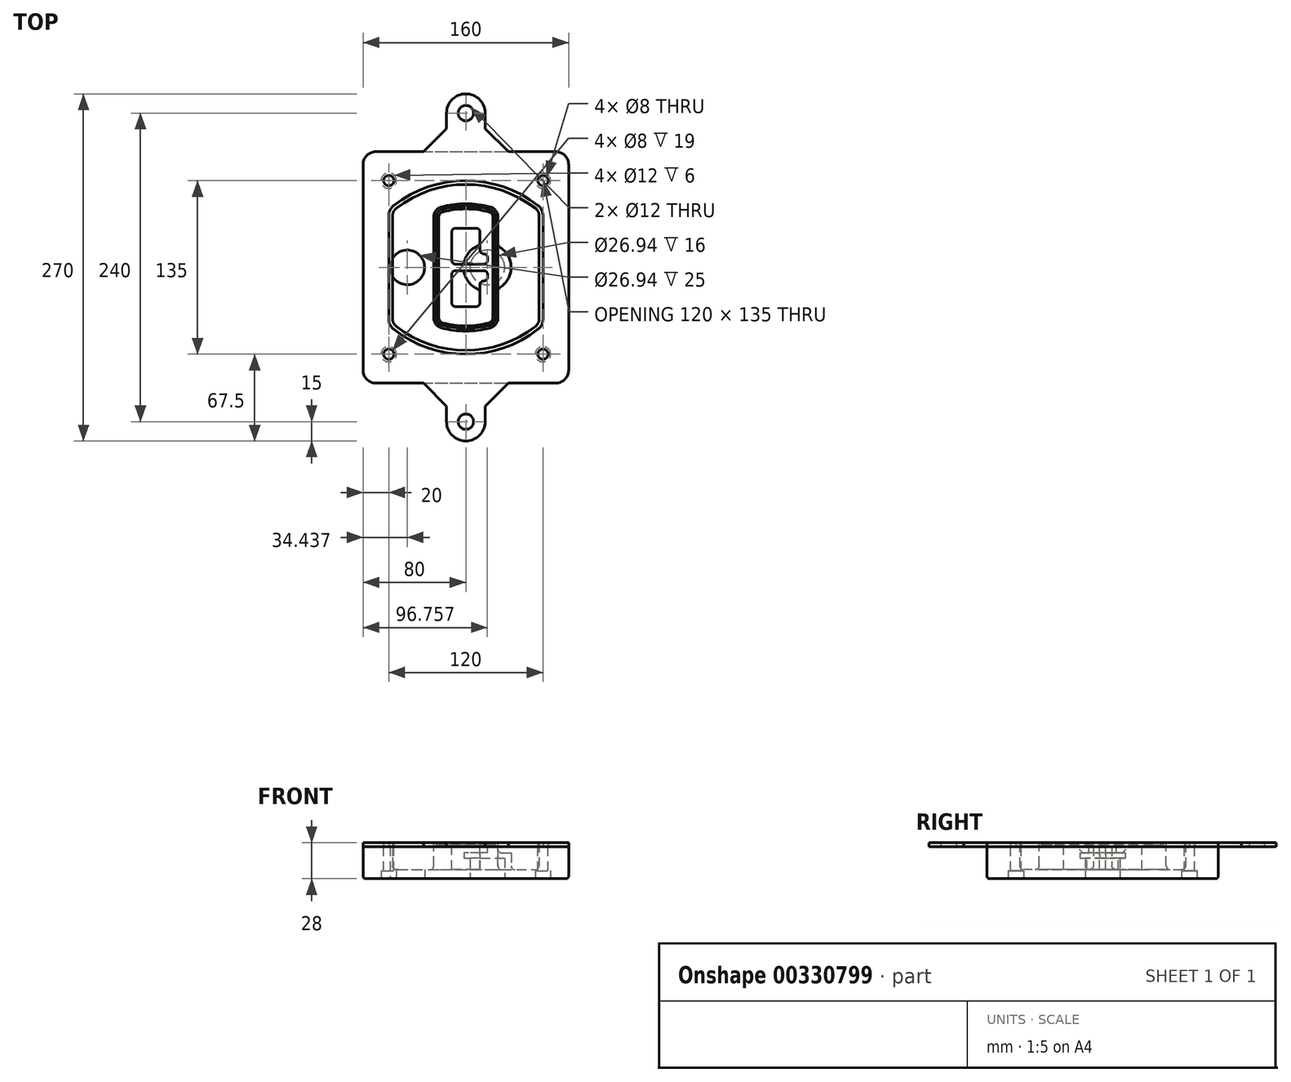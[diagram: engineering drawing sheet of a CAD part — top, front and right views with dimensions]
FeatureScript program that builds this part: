
annotation { "Feature Type Name" : "Feature", "Feature Type Description" : "" }
export const myFeature = defineFeature(function(context is Context, id is Id, definition is map)
    precondition{}
    {
        {
            var Q0;
            Q0=qCreatedBy(makeId("Top.planeOp"),FACE);
            var sketch = newSketch(context, id + "F0", { "sketchPlane" : qUnion([Q0])});
            skPoint(sketch, "E0.rect.middle", {"position": v(0, 0) * mm});
            skLineSegment(sketch, "E1.bottom", {"start": v(-70, -90) * mm, "end": v(70, -90) * mm});
            skLineSegment(sketch, "E1.top", {"start": v(-70, 90) * mm, "end": v(70, 90) * mm});
            skLineSegment(sketch, "E1.left", {"start": v(-80, -80) * mm, "end": v(-80, 80) * mm});
            skLineSegment(sketch, "E1.right", {"start": v(80, -80) * mm, "end": v(80, 80) * mm});
            skLineSegment(sketch, "E2", {"start": v(-80, 90) * mm, "end": v(80, -90) * mm, "construction": true});
            skLineSegment(sketch, "E3", {"start": v(80, 90) * mm, "end": v(-80, -90) * mm, "construction": true});
            skCircle(sketch, "E4", {"center": v(-60, 67.5) * mm, "radius": 4 * mm});
            skCircle(sketch, "E5", {"center": v(60, 67.5) * mm, "radius": 4 * mm});
            skCircle(sketch, "E6", {"center": v(60, -67.5) * mm, "radius": 4 * mm});
            skCircle(sketch, "E7", {"center": v(-60, -67.5) * mm, "radius": 4 * mm});
            skLineSegment(sketch, "E8", {"start": v(-60, 67.5) * mm, "end": v(60, 67.5) * mm, "construction": true});
            skLineSegment(sketch, "E9", {"start": v(60, 67.5) * mm, "end": v(60, -67.5) * mm, "construction": true});
            skLineSegment(sketch, "E10", {"start": v(60, -67.5) * mm, "end": v(-60, -67.5) * mm, "construction": true});
            skLineSegment(sketch, "E11", {"start": v(-60, -67.5) * mm, "end": v(-60, 67.5) * mm, "construction": true});
            skLineSegment(sketch, "E12", {"start": v(-60, 40.3) * mm, "end": v(-60, -40.3) * mm});
            skLineSegment(sketch, "E13", {"start": v(60, 40.3) * mm, "end": v(60, -40.3) * mm});
            skArc(sketch, "E14", {"start": v(56.15, 48.18) * mm, "mid": v(0, 67.5) * mm, "end": v(-56.15, 48.18) * mm});
            skArc(sketch, "E15", {"start": v(-56.15, -48.18) * mm, "mid": v(0, -67.5) * mm, "end": v(56.15, -48.18) * mm});
            skLineSegment(sketch, "E16", {"start": v(-60, 0) * mm, "end": v(60, 0) * mm, "construction": true});
            skPoint(sketch, "E17.visualSharp", {"position": v(-60, -45) * mm});
            skArc(sketch, "E17.filletArc", {"start": v(-60, -40.3) * mm, "mid": v(-58.99, -44.68) * mm, "end": v(-56.15, -48.18) * mm});
            skPoint(sketch, "E18.visualSharp", {"position": v(-60, 45) * mm});
            skArc(sketch, "E18.filletArc", {"start": v(-56.15, 48.18) * mm, "mid": v(-58.99, 44.68) * mm, "end": v(-60, 40.3) * mm});
            skPoint(sketch, "E19.visualSharp", {"position": v(60, 45) * mm});
            skArc(sketch, "E19.filletArc", {"start": v(60, 40.3) * mm, "mid": v(58.99, 44.68) * mm, "end": v(56.15, 48.18) * mm});
            skPoint(sketch, "E20.visualSharp", {"position": v(60, -45) * mm});
            skArc(sketch, "E20.filletArc", {"start": v(56.15, -48.18) * mm, "mid": v(58.99, -44.68) * mm, "end": v(60, -40.3) * mm});
            skPoint(sketch, "E21.visualSharp", {"position": v(-80, 90) * mm});
            skArc(sketch, "E21.filletArc", {"start": v(-70, 90) * mm, "mid": v(-77.07, 87.07) * mm, "end": v(-80, 80) * mm});
            skPoint(sketch, "E22.visualSharp", {"position": v(80, 90) * mm});
            skArc(sketch, "E22.filletArc", {"start": v(80, 80) * mm, "mid": v(77.07, 87.07) * mm, "end": v(70, 90) * mm});
            skPoint(sketch, "E23.visualSharp", {"position": v(80, -90) * mm});
            skArc(sketch, "E23.filletArc", {"start": v(70, -90) * mm, "mid": v(77.07, -87.07) * mm, "end": v(80, -80) * mm});
            skPoint(sketch, "E24.visualSharp", {"position": v(-80, -90) * mm});
            skArc(sketch, "E24.filletArc", {"start": v(-80, -80) * mm, "mid": v(-77.07, -87.07) * mm, "end": v(-70, -90) * mm});
            skArc(sketch, "E25.0", {"start": v(57, 40.3) * mm, "mid": v(56.3, 43.36) * mm, "end": v(54.3, 45.81) * mm});
            skLineSegment(sketch, "E25.1", {"start": v(57, 40.3) * mm, "end": v(57, -40.3) * mm});
            skArc(sketch, "E25.2", {"start": v(54.3, -45.81) * mm, "mid": v(56.3, -43.36) * mm, "end": v(57, -40.3) * mm});
            skArc(sketch, "E25.3", {"start": v(-54.3, -45.81) * mm, "mid": v(0, -64.5) * mm, "end": v(54.3, -45.81) * mm});
            skArc(sketch, "E25.4", {"start": v(-57, -40.3) * mm, "mid": v(-56.3, -43.36) * mm, "end": v(-54.3, -45.81) * mm});
            skArc(sketch, "E25.5", {"start": v(54.3, 45.81) * mm, "mid": v(0, 64.5) * mm, "end": v(-54.3, 45.81) * mm});
            skLineSegment(sketch, "E25.6", {"start": v(-57, 40.3) * mm, "end": v(-57, -40.3) * mm});
            skArc(sketch, "E25.7", {"start": v(-54.3, 45.81) * mm, "mid": v(-56.3, 43.36) * mm, "end": v(-57, 40.3) * mm});
            skArc(sketch, "E26.0", {"start": v(-58.62, 51.33) * mm, "mid": v(-62.58, 46.43) * mm, "end": v(-64, 40.3) * mm});
            skArc(sketch, "E26.1", {"start": v(58.62, 51.33) * mm, "mid": v(0, 71.5) * mm, "end": v(-58.62, 51.33) * mm});
            skArc(sketch, "E26.2", {"start": v(64, 40.3) * mm, "mid": v(62.58, 46.43) * mm, "end": v(58.62, 51.33) * mm});
            skLineSegment(sketch, "E26.3", {"start": v(64, 40.3) * mm, "end": v(64, -40.3) * mm});
            skArc(sketch, "E26.4", {"start": v(58.62, -51.33) * mm, "mid": v(62.58, -46.43) * mm, "end": v(64, -40.3) * mm});
            skLineSegment(sketch, "E26.5", {"start": v(-64, 40.3) * mm, "end": v(-64, -40.3) * mm});
            skArc(sketch, "E26.6", {"start": v(-58.62, -51.33) * mm, "mid": v(0, -71.5) * mm, "end": v(58.62, -51.33) * mm});
            skArc(sketch, "E26.7", {"start": v(-64, -40.3) * mm, "mid": v(-62.58, -46.43) * mm, "end": v(-58.62, -51.33) * mm});
            skSolve(sketch);
        }
        {
            var Q0;
            Q0=makeQuery(id+"F0.imprint","IMPRINT",FACE,{"disambiguationData":[TD([[makeQuery(id+"F0.imprint","IMPRINT",EDGE,{"derivedFrom":sQuery(id+"F0.wireOp",EDGE,"E1.bottom")}),1.0]])]});
            var Q1;
            Q1=makeQuery(id+"F0.imprint","IMPRINT",FACE,{"disambiguationData":[TD([[makeQuery(id+"F0.imprint","IMPRINT",EDGE,{"derivedFrom":sQuery(id+"F0.wireOp",EDGE,"E12")}),1.0]])]});
            var Q2;
            Q2=makeQuery(id+"F0.imprint","IMPRINT",FACE,{"disambiguationData":[TD([[makeQuery(id+"F0.imprint","IMPRINT",EDGE,{"derivedFrom":sQuery(id+"F0.wireOp",EDGE,"E25.0")}),1.0]])]});
            var Q3;
            Q3=makeQuery(id+"F0.imprint","IMPRINT",FACE,{"disambiguationData":[TD([[makeQuery(id+"F0.imprint","IMPRINT",EDGE,{"derivedFrom":sQuery(id+"F0.wireOp",EDGE,"E12")}),-1.0]])]});
            extrude(context, id + "F1", {"entities" : qUnion([Q0, Q1, Q2, Q3]), "oppositeDirection" : true, "depth" : 25 * mm});
        }
        {
            var Q0;
            Q0=makeQuery(id+"F0.imprint","IMPRINT",FACE,{"disambiguationData":[TD([[makeQuery(id+"F0.imprint","IMPRINT",EDGE,{"derivedFrom":sQuery(id+"F0.wireOp",EDGE,"E12")}),1.0]])]});
            extrude(context, id + "F2", {"entities" : qUnion([Q0]), "operationType" : NewBodyOperationType.ADD, "depth" : 3 * mm});
        }
        {
            var Q0;
            Q0=makeQuery(id+"F0.imprint","IMPRINT",FACE,{"disambiguationData":[TD([[makeQuery(id+"F0.imprint","IMPRINT",EDGE,{"derivedFrom":sQuery(id+"F0.wireOp",EDGE,"E25.0")}),1.0]])]});
            extrude(context, id + "F3", {"entities" : qUnion([Q0]), "operationType" : NewBodyOperationType.REMOVE, "oppositeDirection" : true, "depth" : 18 * mm});
        }
        {
            var Q0;
            Q0=makeQuery(id+"F2.opExtrude","CAP_FACE",FACE,{"disambiguationData":[OSD([sQuery(id+"F0.wireOp",EDGE,"E12"),sQuery(id+"F0.wireOp",EDGE,"E13"),sQuery(id+"F0.wireOp",EDGE,"E14"),sQuery(id+"F0.wireOp",EDGE,"E15"),sQuery(id+"F0.wireOp",EDGE,"E17.filletArc"),sQuery(id+"F0.wireOp",EDGE,"E18.filletArc"),sQuery(id+"F0.wireOp",EDGE,"E19.filletArc"),sQuery(id+"F0.wireOp",EDGE,"E20.filletArc"),sQuery(id+"F0.wireOp",EDGE,"E25.0"),sQuery(id+"F0.wireOp",EDGE,"E25.1"),sQuery(id+"F0.wireOp",EDGE,"E25.2"),sQuery(id+"F0.wireOp",EDGE,"E25.3"),sQuery(id+"F0.wireOp",EDGE,"E25.4"),sQuery(id+"F0.wireOp",EDGE,"E25.5"),sQuery(id+"F0.wireOp",EDGE,"E25.6"),sQuery(id+"F0.wireOp",EDGE,"E25.7")])],"isStart":false});
            var sketch = newSketch(context, id + "F4", { "sketchPlane" : qUnion([Q0])});
            skArc(sketch, "E27.0", {"start": v(-19.08, -46.97) * mm, "mid": v(0, -49.5) * mm, "end": v(19.08, -46.97) * mm});
            skArc(sketch, "E28.0", {"start": v(19.08, 46.97) * mm, "mid": v(0, 49.5) * mm, "end": v(-19.08, 46.97) * mm});
            skLineSegment(sketch, "E29", {"start": v(-25, 39.25) * mm, "end": v(-25, -39.25) * mm});
            skLineSegment(sketch, "E30", {"start": v(25, 39.25) * mm, "end": v(25, -39.25) * mm});
            skLineSegment(sketch, "E31", {"start": v(-25, 45.1) * mm, "end": v(25, 45.1) * mm, "construction": true});
            skLineSegment(sketch, "E32", {"start": v(-25, -45.1) * mm, "end": v(25, -45.1) * mm, "construction": true});
            skPoint(sketch, "E33.visualSharp", {"position": v(-25, 45.1) * mm});
            skArc(sketch, "E33.filletArc", {"start": v(-19.08, 46.97) * mm, "mid": v(-23.35, 44.11) * mm, "end": v(-25, 39.25) * mm});
            skPoint(sketch, "E34.visualSharp", {"position": v(25, 45.1) * mm});
            skArc(sketch, "E34.filletArc", {"start": v(25, 39.25) * mm, "mid": v(23.35, 44.11) * mm, "end": v(19.08, 46.97) * mm});
            skPoint(sketch, "E35.visualSharp", {"position": v(25, -45.1) * mm});
            skArc(sketch, "E35.filletArc", {"start": v(19.08, -46.97) * mm, "mid": v(23.35, -44.11) * mm, "end": v(25, -39.25) * mm});
            skPoint(sketch, "E36.visualSharp", {"position": v(-25, -45.1) * mm});
            skArc(sketch, "E36.filletArc", {"start": v(-25, -39.25) * mm, "mid": v(-23.35, -44.11) * mm, "end": v(-19.08, -46.97) * mm});
            skArc(sketch, "E37.0", {"start": v(54.3, 45.81) * mm, "mid": v(0, 64.5) * mm, "end": v(-54.3, 45.81) * mm});
            skArc(sketch, "E37.1", {"start": v(-54.3, 45.81) * mm, "mid": v(-56.3, 43.36) * mm, "end": v(-57, 40.3) * mm});
            skLineSegment(sketch, "E37.2", {"start": v(-57, 40.3) * mm, "end": v(-57, -40.3) * mm});
            skArc(sketch, "E37.3", {"start": v(-57, -40.3) * mm, "mid": v(-56.3, -43.36) * mm, "end": v(-54.3, -45.81) * mm});
            skArc(sketch, "E37.4", {"start": v(-54.3, -45.81) * mm, "mid": v(0, -64.5) * mm, "end": v(54.3, -45.81) * mm});
            skArc(sketch, "E37.5", {"start": v(54.3, -45.81) * mm, "mid": v(56.3, -43.36) * mm, "end": v(57, -40.3) * mm});
            skLineSegment(sketch, "E37.6", {"start": v(57, 40.3) * mm, "end": v(57, -40.3) * mm});
            skArc(sketch, "E37.7", {"start": v(57, 40.3) * mm, "mid": v(56.3, 43.36) * mm, "end": v(54.3, 45.81) * mm});
            skLineSegment(sketch, "E38.0", {"start": v(23, 39.25) * mm, "end": v(23, -39.25) * mm});
            skArc(sketch, "E38.1", {"start": v(18.56, -45.04) * mm, "mid": v(21.76, -42.9) * mm, "end": v(23, -39.25) * mm});
            skArc(sketch, "E38.2", {"start": v(-18.56, -45.04) * mm, "mid": v(0, -47.5) * mm, "end": v(18.56, -45.04) * mm});
            skArc(sketch, "E38.3", {"start": v(-23, -39.25) * mm, "mid": v(-21.76, -42.9) * mm, "end": v(-18.56, -45.04) * mm});
            skLineSegment(sketch, "E38.4", {"start": v(-23, 39.25) * mm, "end": v(-23, -39.25) * mm});
            skArc(sketch, "E38.5", {"start": v(23, 39.25) * mm, "mid": v(21.76, 42.9) * mm, "end": v(18.56, 45.04) * mm});
            skArc(sketch, "E38.6", {"start": v(-18.56, 45.04) * mm, "mid": v(-21.76, 42.9) * mm, "end": v(-23, 39.25) * mm});
            skArc(sketch, "E38.7", {"start": v(18.56, 45.04) * mm, "mid": v(0, 47.5) * mm, "end": v(-18.56, 45.04) * mm});
            skArc(sketch, "E39.0", {"start": v(21, 39.25) * mm, "mid": v(20.18, 41.68) * mm, "end": v(18.04, 43.1) * mm});
            skLineSegment(sketch, "E39.1", {"start": v(21, 39.25) * mm, "end": v(21, -39.25) * mm});
            skArc(sketch, "E39.2", {"start": v(18.04, -43.1) * mm, "mid": v(20.18, -41.68) * mm, "end": v(21, -39.25) * mm});
            skArc(sketch, "E39.3", {"start": v(-18.04, -43.1) * mm, "mid": v(0, -45.5) * mm, "end": v(18.04, -43.1) * mm});
            skArc(sketch, "E39.4", {"start": v(-21, -39.25) * mm, "mid": v(-20.18, -41.68) * mm, "end": v(-18.04, -43.1) * mm});
            skArc(sketch, "E39.5", {"start": v(18.04, 43.1) * mm, "mid": v(0, 45.5) * mm, "end": v(-18.04, 43.1) * mm});
            skLineSegment(sketch, "E39.6", {"start": v(-21, 39.25) * mm, "end": v(-21, -39.25) * mm});
            skArc(sketch, "E39.7", {"start": v(-18.04, 43.1) * mm, "mid": v(-20.18, 41.68) * mm, "end": v(-21, 39.25) * mm});
            skLineSegment(sketch, "E40", {"start": v(-25, 0) * mm, "end": v(25, 0) * mm, "construction": true});
            skLineSegment(sketch, "E41", {"start": v(-11, 5.5) * mm, "end": v(-11, 27.5) * mm});
            skLineSegment(sketch, "E42", {"start": v(-8, 30.5) * mm, "end": v(8, 30.5) * mm});
            skLineSegment(sketch, "E43", {"start": v(11, 27.5) * mm, "end": v(11, 13.5) * mm});
            skLineSegment(sketch, "E44", {"start": v(14, 10.5) * mm, "end": v(14, 10.5) * mm});
            skLineSegment(sketch, "E45", {"start": v(17, 7.5) * mm, "end": v(17, 5.5) * mm});
            skLineSegment(sketch, "E46", {"start": v(14, 2.5) * mm, "end": v(-8, 2.5) * mm});
            skPoint(sketch, "E47.visualSharp", {"position": v(-11, 30.5) * mm});
            skArc(sketch, "E47.filletArc", {"start": v(-8, 30.5) * mm, "mid": v(-10.12, 29.62) * mm, "end": v(-11, 27.5) * mm});
            skPoint(sketch, "E48.visualSharp", {"position": v(11, 30.5) * mm});
            skArc(sketch, "E48.filletArc", {"start": v(11, 27.5) * mm, "mid": v(10.12, 29.62) * mm, "end": v(8, 30.5) * mm});
            skPoint(sketch, "E49.visualSharp", {"position": v(11, 10.5) * mm});
            skArc(sketch, "E49.filletArc", {"start": v(11, 13.5) * mm, "mid": v(11.88, 11.38) * mm, "end": v(14, 10.5) * mm});
            skPoint(sketch, "E50.visualSharp", {"position": v(17, 10.5) * mm});
            skArc(sketch, "E50.filletArc", {"start": v(17, 7.5) * mm, "mid": v(16.12, 9.62) * mm, "end": v(14, 10.5) * mm});
            skPoint(sketch, "E51.visualSharp", {"position": v(17, 2.5) * mm});
            skArc(sketch, "E51.filletArc", {"start": v(14, 2.5) * mm, "mid": v(16.12, 3.38) * mm, "end": v(17, 5.5) * mm});
            skPoint(sketch, "E52.visualSharp", {"position": v(-11, 2.5) * mm});
            skArc(sketch, "E52.filletArc", {"start": v(-11, 5.5) * mm, "mid": v(-10.12, 3.38) * mm, "end": v(-8, 2.5) * mm});
            skLineSegment(sketch, "E53.0.MirrorCS", {"start": v(14, -2.5) * mm, "end": v(-8, -2.5) * mm});
            skArc(sketch, "E54.0.MirrorCS", {"start": v(-11, -5.5) * mm, "mid": v(-10.12, -3.38) * mm, "end": v(-8, -2.5) * mm});
            skLineSegment(sketch, "E55.0.MirrorCS", {"start": v(-11, -5.5) * mm, "end": v(-11, -27.5) * mm});
            skArc(sketch, "E56.0.MirrorCS", {"start": v(-8, -30.5) * mm, "mid": v(-10.12, -29.62) * mm, "end": v(-11, -27.5) * mm});
            skLineSegment(sketch, "E57.0.MirrorCS", {"start": v(-8, -30.5) * mm, "end": v(8, -30.5) * mm});
            skArc(sketch, "E58.0.MirrorCS", {"start": v(11, -27.5) * mm, "mid": v(10.12, -29.62) * mm, "end": v(8, -30.5) * mm});
            skLineSegment(sketch, "E59.0.MirrorCS", {"start": v(11, -27.5) * mm, "end": v(11, -13.5) * mm});
            skArc(sketch, "E60.0.MirrorCS", {"start": v(11, -13.5) * mm, "mid": v(11.88, -11.38) * mm, "end": v(14, -10.5) * mm});
            skArc(sketch, "E61.0.MirrorCS", {"start": v(17, -7.5) * mm, "mid": v(16.12, -9.62) * mm, "end": v(14, -10.5) * mm});
            skLineSegment(sketch, "E62.0.MirrorCS", {"start": v(17, -7.5) * mm, "end": v(17, -5.5) * mm});
            skArc(sketch, "E63.0.MirrorCS", {"start": v(14, -2.5) * mm, "mid": v(16.12, -3.38) * mm, "end": v(17, -5.5) * mm});
            skSolve(sketch);
        }
        {
            var Q0;
            Q0=makeQuery(id+"F4.imprint","IMPRINT",FACE,{"disambiguationData":[TD([[makeQuery(id+"F4.imprint","IMPRINT",EDGE,{"derivedFrom":sQuery(id+"F4.wireOp",EDGE,"E27.0")}),1.0]])]});
            var Q1;
            Q1=makeQuery(id+"F4.imprint","IMPRINT",FACE,{"disambiguationData":[TD([[makeQuery(id+"F4.imprint","IMPRINT",EDGE,{"derivedFrom":sQuery(id+"F4.wireOp",EDGE,"E38.0")}),-1.0]])]});
            var Q2;
            Q2=makeQuery(id+"F4.imprint","IMPRINT",FACE,{"disambiguationData":[TD([[makeQuery(id+"F4.imprint","IMPRINT",EDGE,{"derivedFrom":sQuery(id+"F4.wireOp",EDGE,"E39.0")}),1.0]])]});
            extrude(context, id + "F5", {"entities" : qUnion([Q0, Q1, Q2]), "operationType" : NewBodyOperationType.ADD, "endBound" : BoundingType.UP_TO_NEXT, "oppositeDirection" : true, "depth" : 25 * mm});
        }
        {
            var Q0;
            Q0=makeQuery(id+"F4.imprint","IMPRINT",FACE,{"disambiguationData":[TD([[makeQuery(id+"F4.imprint","IMPRINT",EDGE,{"derivedFrom":sQuery(id+"F4.wireOp",EDGE,"E38.0")}),-1.0]])]});
            extrude(context, id + "F6", {"entities" : qUnion([Q0]), "operationType" : NewBodyOperationType.REMOVE, "oppositeDirection" : true, "depth" : 2 * mm});
        }
        {
            var Q0;
            Q0=makeQuery(id+"F1.opExtrude","CAP_FACE",FACE,{"disambiguationData":[OSD([sQuery(id+"F0.wireOp",EDGE,"E1.bottom"),sQuery(id+"F0.wireOp",EDGE,"E1.top"),sQuery(id+"F0.wireOp",EDGE,"E1.left"),sQuery(id+"F0.wireOp",EDGE,"E1.right"),sQuery(id+"F0.wireOp",EDGE,"E4"),sQuery(id+"F0.wireOp",EDGE,"E5"),sQuery(id+"F0.wireOp",EDGE,"E6"),sQuery(id+"F0.wireOp",EDGE,"E7"),sQuery(id+"F0.wireOp",EDGE,"E21.filletArc"),sQuery(id+"F0.wireOp",EDGE,"E22.filletArc"),sQuery(id+"F0.wireOp",EDGE,"E23.filletArc"),sQuery(id+"F0.wireOp",EDGE,"E24.filletArc")])],"isStart":false});
            var sketch = newSketch(context, id + "F7", { "sketchPlane" : qUnion([Q0])});
            skCircle(sketch, "E64", {"center": v(16.76, 0) * mm, "radius": 13.47 * mm});
            skCircle(sketch, "E65", {"center": v(-45.56, 0) * mm, "radius": 13.47 * mm});
            skLineSegment(sketch, "E66", {"start": v(80, 0) * mm, "end": v(-80, 0) * mm});
            skCircle(sketch, "E67", {"center": v(16.76, 0) * mm, "radius": 18.47 * mm});
            skCircle(sketch, "E68", {"center": v(60, -67.5) * mm, "radius": 6 * mm});
            skCircle(sketch, "E69", {"center": v(-60, -67.5) * mm, "radius": 6 * mm});
            skCircle(sketch, "E70", {"center": v(-60, 67.5) * mm, "radius": 6 * mm});
            skCircle(sketch, "E71", {"center": v(60, 67.5) * mm, "radius": 6 * mm});
            skSolve(sketch);
        }
        {
            var Q0;
            {var subQ1=sQuery(id+"F7.wireOp",EDGE,"E66");var subQ4=sQuery(id+"F7.wireOp",EDGE,"E64");var subQ6=makeQuery(id+"F7.imprint","INTERSECT",VERTEX,{"disambiguationData":[OD(0.0)],"derivedFrom":[subQ4,subQ1]});Q0=makeQuery(id+"F7.imprint","IMPRINT",FACE,{"disambiguationData":[TD([[makeQuery(id+"F7.imprint","IMPRINT",EDGE,{"disambiguationData":[TD([[subQ6,-1.0]])],"derivedFrom":subQ4}),-1.0]])]});}
            var Q1;
            {var subQ0=sQuery(id+"F7.wireOp",EDGE,"E66");var subQ1=sQuery(id+"F7.wireOp",EDGE,"E64");var subQ3=makeQuery(id+"F7.imprint","INTERSECT",VERTEX,{"disambiguationData":[OD(0.0)],"derivedFrom":[subQ1,subQ0]});Q1=makeQuery(id+"F7.imprint","IMPRINT",FACE,{"disambiguationData":[TD([[makeQuery(id+"F7.imprint","IMPRINT",EDGE,{"disambiguationData":[TD([[subQ3,-1.0]])],"derivedFrom":subQ1}),1.0]])]});}
            var Q2;
            {var subQ0=sQuery(id+"F7.wireOp",EDGE,"E66");var subQ1=sQuery(id+"F7.wireOp",EDGE,"E64");var subQ3=makeQuery(id+"F7.imprint","INTERSECT",VERTEX,{"disambiguationData":[OD(0.0)],"derivedFrom":[subQ1,subQ0]});Q2=makeQuery(id+"F7.imprint","IMPRINT",FACE,{"disambiguationData":[TD([[makeQuery(id+"F7.imprint","IMPRINT",EDGE,{"disambiguationData":[TD([[subQ3,1.0]])],"derivedFrom":subQ1}),1.0]])]});}
            var Q3;
            {var subQ1=sQuery(id+"F7.wireOp",EDGE,"E66");var subQ4=sQuery(id+"F7.wireOp",EDGE,"E64");var subQ6=makeQuery(id+"F7.imprint","INTERSECT",VERTEX,{"disambiguationData":[OD(0.0)],"derivedFrom":[subQ4,subQ1]});Q3=makeQuery(id+"F7.imprint","IMPRINT",FACE,{"disambiguationData":[TD([[makeQuery(id+"F7.imprint","IMPRINT",EDGE,{"disambiguationData":[TD([[subQ6,1.0]])],"derivedFrom":subQ4}),-1.0]])]});}
            extrude(context, id + "F8", {"entities" : qUnion([Q0, Q1, Q2, Q3]), "operationType" : NewBodyOperationType.ADD, "oppositeDirection" : true, "depth" : 20 * mm});
        }
        {
            var Q0;
            {var subQ0=sQuery(id+"F7.wireOp",EDGE,"E66");var subQ1=sQuery(id+"F7.wireOp",EDGE,"E64");var subQ3=makeQuery(id+"F7.imprint","INTERSECT",VERTEX,{"disambiguationData":[OD(0.0)],"derivedFrom":[subQ1,subQ0]});Q0=makeQuery(id+"F7.imprint","IMPRINT",FACE,{"disambiguationData":[TD([[makeQuery(id+"F7.imprint","IMPRINT",EDGE,{"disambiguationData":[TD([[subQ3,-1.0]])],"derivedFrom":subQ1}),1.0]])]});}
            var Q1;
            {var subQ0=sQuery(id+"F7.wireOp",EDGE,"E66");var subQ1=sQuery(id+"F7.wireOp",EDGE,"E64");var subQ3=makeQuery(id+"F7.imprint","INTERSECT",VERTEX,{"disambiguationData":[OD(0.0)],"derivedFrom":[subQ1,subQ0]});Q1=makeQuery(id+"F7.imprint","IMPRINT",FACE,{"disambiguationData":[TD([[makeQuery(id+"F7.imprint","IMPRINT",EDGE,{"disambiguationData":[TD([[subQ3,1.0]])],"derivedFrom":subQ1}),1.0]])]});}
            extrude(context, id + "F9", {"entities" : qUnion([Q0, Q1]), "operationType" : NewBodyOperationType.REMOVE, "oppositeDirection" : true, "depth" : 16 * mm});
        }
        {
            var Q0;
            {var subQ0=sQuery(id+"F7.wireOp",EDGE,"E66");var subQ1=sQuery(id+"F7.wireOp",EDGE,"E65");var subQ3=makeQuery(id+"F7.imprint","INTERSECT",VERTEX,{"disambiguationData":[OD(0.0)],"derivedFrom":[subQ1,subQ0]});Q0=makeQuery(id+"F7.imprint","IMPRINT",FACE,{"disambiguationData":[TD([[makeQuery(id+"F7.imprint","IMPRINT",EDGE,{"disambiguationData":[TD([[subQ3,-1.0]])],"derivedFrom":subQ1}),1.0]])]});}
            var Q1;
            {var subQ0=sQuery(id+"F7.wireOp",EDGE,"E66");var subQ1=sQuery(id+"F7.wireOp",EDGE,"E65");var subQ3=makeQuery(id+"F7.imprint","INTERSECT",VERTEX,{"disambiguationData":[OD(0.0)],"derivedFrom":[subQ1,subQ0]});Q1=makeQuery(id+"F7.imprint","IMPRINT",FACE,{"disambiguationData":[TD([[makeQuery(id+"F7.imprint","IMPRINT",EDGE,{"disambiguationData":[TD([[subQ3,1.0]])],"derivedFrom":subQ1}),1.0]])]});}
            extrude(context, id + "F10", {"entities" : qUnion([Q0, Q1]), "operationType" : NewBodyOperationType.REMOVE, "oppositeDirection" : true, "depth" : 25 * mm});
        }
        {
            var Q0;
            Q0=makeQuery(id+"F7.imprint","IMPRINT",FACE,{"disambiguationData":[TD([[makeQuery(id+"F7.imprint","IMPRINT",EDGE,{"derivedFrom":sQuery(id+"F7.wireOp",EDGE,"E68")}),1.0]])]});
            var Q1;
            Q1=makeQuery(id+"F7.imprint","IMPRINT",FACE,{"disambiguationData":[TD([[makeQuery(id+"F7.imprint","IMPRINT",EDGE,{"derivedFrom":makeQuery(id+"F1.opExtrude","CAP_EDGE",EDGE,{"disambiguationData":[OSD([sQuery(id+"F0.wireOp",EDGE,"E5")])],"isStart":false})}),-1.0]])]});
            var Q2;
            Q2=makeQuery(id+"F7.imprint","IMPRINT",FACE,{"disambiguationData":[TD([[makeQuery(id+"F7.imprint","IMPRINT",EDGE,{"derivedFrom":sQuery(id+"F7.wireOp",EDGE,"E69")}),1.0]])]});
            var Q3;
            Q3=makeQuery(id+"F7.imprint","IMPRINT",FACE,{"disambiguationData":[TD([[makeQuery(id+"F7.imprint","IMPRINT",EDGE,{"derivedFrom":makeQuery(id+"F1.opExtrude","CAP_EDGE",EDGE,{"disambiguationData":[OSD([sQuery(id+"F0.wireOp",EDGE,"E4")])],"isStart":false})}),-1.0]])]});
            var Q4;
            Q4=makeQuery(id+"F7.imprint","IMPRINT",FACE,{"disambiguationData":[TD([[makeQuery(id+"F7.imprint","IMPRINT",EDGE,{"derivedFrom":sQuery(id+"F7.wireOp",EDGE,"E70")}),1.0]])]});
            var Q5;
            Q5=makeQuery(id+"F7.imprint","IMPRINT",FACE,{"disambiguationData":[TD([[makeQuery(id+"F7.imprint","IMPRINT",EDGE,{"derivedFrom":makeQuery(id+"F1.opExtrude","CAP_EDGE",EDGE,{"disambiguationData":[OSD([sQuery(id+"F0.wireOp",EDGE,"E7")])],"isStart":false})}),-1.0]])]});
            var Q6;
            Q6=makeQuery(id+"F7.imprint","IMPRINT",FACE,{"disambiguationData":[TD([[makeQuery(id+"F7.imprint","IMPRINT",EDGE,{"derivedFrom":sQuery(id+"F7.wireOp",EDGE,"E71")}),1.0]])]});
            var Q7;
            Q7=makeQuery(id+"F7.imprint","IMPRINT",FACE,{"disambiguationData":[TD([[makeQuery(id+"F7.imprint","IMPRINT",EDGE,{"derivedFrom":makeQuery(id+"F1.opExtrude","CAP_EDGE",EDGE,{"disambiguationData":[OSD([sQuery(id+"F0.wireOp",EDGE,"E6")])],"isStart":false})}),-1.0]])]});
            extrude(context, id + "F11", {"entities" : qUnion([Q0, Q1, Q2, Q3, Q4, Q5, Q6, Q7]), "operationType" : NewBodyOperationType.REMOVE, "oppositeDirection" : true, "depth" : 6 * mm});
        }
        {
            var Q0;
            Q0=makeQuery(id+"F9.boolean.opBoolean","COPY",FACE,{"derivedFrom":makeQuery(id+"F9.opExtrude","CAP_FACE",FACE,{"disambiguationData":[OSD([sQuery(id+"F7.wireOp",EDGE,"E64")])],"isStart":false})});
            var sketch = newSketch(context, id + "F12", { "sketchPlane" : qUnion([Q0])});
            skArc(sketch, "E72.0", {"start": v(11, 17.55) * mm, "mid": v(2.57, 11.82) * mm, "end": v(-1.54, 2.5) * mm});
            skArc(sketch, "E72.1", {"start": v(-1.54, -2.5) * mm, "mid": v(2.57, -11.82) * mm, "end": v(11, -17.55) * mm});
            skLineSegment(sketch, "E73", {"start": v(-1.54, -2.5) * mm, "end": v(14, -2.5) * mm});
            skLineSegment(sketch, "E74.0", {"start": v(14, 2.5) * mm, "end": v(-1.54, 2.5) * mm});
            skArc(sketch, "E74.1", {"start": v(14, 2.5) * mm, "mid": v(16.12, 3.38) * mm, "end": v(17, 5.5) * mm});
            skLineSegment(sketch, "E74.2", {"start": v(17, 7.5) * mm, "end": v(17, 5.5) * mm});
            skArc(sketch, "E74.3", {"start": v(17, 7.5) * mm, "mid": v(16.12, 9.62) * mm, "end": v(14, 10.5) * mm});
            skArc(sketch, "E74.4", {"start": v(11, 13.5) * mm, "mid": v(11.88, 11.38) * mm, "end": v(14, 10.5) * mm});
            skLineSegment(sketch, "E74.5", {"start": v(11, 17.55) * mm, "end": v(11, 13.5) * mm});
            skLineSegment(sketch, "E74.7", {"start": v(14, -2.5) * mm, "end": v(-1.54, -2.5) * mm});
            skArc(sketch, "E74.8", {"start": v(14, -2.5) * mm, "mid": v(16.12, -3.38) * mm, "end": v(17, -5.5) * mm});
            skLineSegment(sketch, "E74.9", {"start": v(17, -7.5) * mm, "end": v(17, -5.5) * mm});
            skArc(sketch, "E74.10", {"start": v(17, -7.5) * mm, "mid": v(16.12, -9.62) * mm, "end": v(14, -10.5) * mm});
            skArc(sketch, "E74.11", {"start": v(11, -13.5) * mm, "mid": v(11.88, -11.38) * mm, "end": v(14, -10.5) * mm});
            skLineSegment(sketch, "E74.12", {"start": v(11, -17.55) * mm, "end": v(11, -13.5) * mm});
            skPoint(sketch, "E75.orphan", {"position": v(11, -27.5) * mm});
            skPoint(sketch, "E76.orphan", {"position": v(-8, -2.5) * mm});
            skPoint(sketch, "E77.orphan", {"position": v(-8, 2.5) * mm});
            skPoint(sketch, "E78.orphan", {"position": v(11, 27.5) * mm});
            skSolve(sketch);
        }
        {
            var Q0;
            {var subQ7=sQuery(id+"F12.wireOp",EDGE,"E72.0");var subQ14=sQuery(id+"F12.wireOp",EDGE,"E72.1");var subQ16=sQuery(id+"F12.wireOp",EDGE,"E74.1");var subQ18=sQuery(id+"F12.wireOp",EDGE,"E74.8");Q0=qUnion([makeQuery(id+"F12.imprint","IMPRINT",FACE,{"disambiguationData":[TD([[makeQuery(id+"F12.imprint","IMPRINT",EDGE,{"derivedFrom":subQ7}),1.0]])]}),makeQuery(id+"F12.imprint","IMPRINT",FACE,{"disambiguationData":[TD([[makeQuery(id+"F12.imprint","IMPRINT",EDGE,{"derivedFrom":subQ14}),1.0]])]}),makeQuery(id+"F12.imprint","IMPRINT",FACE,{"disambiguationData":[TD([[makeQuery(id+"F12.imprint","IMPRINT",EDGE,{"derivedFrom":subQ16}),1.0]])]}),makeQuery(id+"F12.imprint","IMPRINT",FACE,{"disambiguationData":[TD([[makeQuery(id+"F12.imprint","IMPRINT",EDGE,{"derivedFrom":subQ18}),-1.0]])]})]);}
            var Q1;
            Q1=makeQuery(id+"F5.boolean.opBoolean","SPLIT",FACE,{"disambiguationData":[TD([makeQuery(id+"F5.opExtrude","SWEPT_FACE",FACE,{"disambiguationData":[OSD([sQuery(id+"F4.wireOp",EDGE,"E41")])]})])],"derivedFrom":makeQuery(id+"F3.boolean.opBoolean","COPY",FACE,{"derivedFrom":makeQuery(id+"F3.opExtrude","CAP_FACE",FACE,{"disambiguationData":[OSD([sQuery(id+"F0.wireOp",EDGE,"E25.0"),sQuery(id+"F0.wireOp",EDGE,"E25.1"),sQuery(id+"F0.wireOp",EDGE,"E25.2"),sQuery(id+"F0.wireOp",EDGE,"E25.3"),sQuery(id+"F0.wireOp",EDGE,"E25.4"),sQuery(id+"F0.wireOp",EDGE,"E25.5"),sQuery(id+"F0.wireOp",EDGE,"E25.6"),sQuery(id+"F0.wireOp",EDGE,"E25.7")])],"isStart":false})})});
            extrude(context, id + "F13", {"entities" : qUnion([Q0]), "operationType" : NewBodyOperationType.REMOVE, "endBound" : BoundingType.UP_TO_SURFACE, "endBoundEntityFace" : qUnion([Q1]), "depth" : 25 * mm});
        }
        {
            var Q0;
            Q0=makeQuery(id+"F3.boolean.opBoolean","COPY",EDGE,{"derivedFrom":makeQuery(id+"F3.opExtrude","CAP_EDGE",EDGE,{"disambiguationData":[OSD([sQuery(id+"F0.wireOp",EDGE,"E25.6")])],"isStart":false})});
            var Q1;
            Q1=makeQuery(id+"F8.boolean.opBoolean","INTERSECT",EDGE,{"derivedFrom":[makeQuery(id+"F5.opExtrude","SWEPT_FACE",FACE,{"disambiguationData":[OSD([sQuery(id+"F4.wireOp",EDGE,"E30")])]}),makeQuery(id+"F8.opExtrude","CAP_FACE",FACE,{"disambiguationData":[OSD([sQuery(id+"F7.wireOp",EDGE,"E67")])],"isStart":false})]});
            var Q2;
            Q2=makeQuery(id+"F8.boolean.opBoolean","INTERSECT",EDGE,{"disambiguationData":[OD(1.0)],"derivedFrom":[makeQuery(id+"F5.opExtrude","SWEPT_FACE",FACE,{"disambiguationData":[OSD([sQuery(id+"F4.wireOp",EDGE,"E30")])]}),makeQuery(id+"F8.opExtrude","SWEPT_FACE",FACE,{"disambiguationData":[OSD([sQuery(id+"F7.wireOp",EDGE,"E67")])]})]});
            var Q3;
            {var subQ0=sQuery(id+"F4.wireOp",EDGE,"E30");Q3=makeQuery(id+"F8.boolean.opBoolean","SPLIT",EDGE,{"disambiguationData":[TD([makeQuery(id+"F5.opExtrude","SWEPT_FACE",FACE,{"disambiguationData":[OSD([sQuery(id+"F4.wireOp",EDGE,"E35.filletArc")])]})])],"derivedFrom":makeQuery(id+"F5.opExtrude","CAP_EDGE",EDGE,{"disambiguationData":[OSD([subQ0])],"isStart":false})});}
            var Q4;
            {var subQ0=sQuery(id+"F0.wireOp",EDGE,"E25.7");var subQ1=sQuery(id+"F0.wireOp",EDGE,"E25.1");var subQ2=sQuery(id+"F0.wireOp",EDGE,"E25.6");var subQ3=sQuery(id+"F0.wireOp",EDGE,"E25.5");var subQ4=sQuery(id+"F0.wireOp",EDGE,"E25.4");var subQ5=sQuery(id+"F0.wireOp",EDGE,"E25.0");var subQ6=sQuery(id+"F0.wireOp",EDGE,"E25.2");var subQ7=sQuery(id+"F0.wireOp",EDGE,"E25.3");Q4=makeQuery(id+"F8.boolean.opBoolean","INTERSECT",EDGE,{"derivedFrom":[makeQuery(id+"F5.boolean.opBoolean","SPLIT",FACE,{"disambiguationData":[TD([makeQuery(id+"F2.opExtrude","SWEPT_FACE",FACE,{"disambiguationData":[OSD([subQ5])]})])],"derivedFrom":makeQuery(id+"F3.boolean.opBoolean","COPY",FACE,{"derivedFrom":makeQuery(id+"F3.opExtrude","CAP_FACE",FACE,{"disambiguationData":[OSD([subQ5,subQ1,subQ6,subQ7,subQ4,subQ3,subQ2,subQ0])],"isStart":false})})}),makeQuery(id+"F8.opExtrude","SWEPT_FACE",FACE,{"disambiguationData":[OSD([sQuery(id+"F7.wireOp",EDGE,"E67")])]})]});}
            var Q5;
            Q5=makeQuery(id+"F8.boolean.opBoolean","INTERSECT",EDGE,{"disambiguationData":[OD(0.0)],"derivedFrom":[makeQuery(id+"F5.opExtrude","SWEPT_FACE",FACE,{"disambiguationData":[OSD([sQuery(id+"F4.wireOp",EDGE,"E30")])]}),makeQuery(id+"F8.opExtrude","SWEPT_FACE",FACE,{"disambiguationData":[OSD([sQuery(id+"F7.wireOp",EDGE,"E67")])]})]});
            fillet(context, id + "F14", {"entities" : qUnion([Q0, Q1, Q2, Q3, Q4, Q5]), "radius" : 3 * mm, "tangentPropagation" : true, "allowEdgeOverflow" : false});
        }
        {
            var Q0;
            Q0=makeQuery(id+"F1.opExtrude","CAP_EDGE",EDGE,{"disambiguationData":[OSD([sQuery(id+"F0.wireOp",EDGE,"E1.bottom")])],"isStart":false});
            fillet(context, id + "F15", {"entities" : qUnion([Q0]), "radius" : 2 * mm, "tangentPropagation" : true, "allowEdgeOverflow" : false});
        }
        {
            var Q0;
            {var subQ0=sQuery(id+"F0.wireOp",EDGE,"E21.filletArc");var subQ1=sQuery(id+"F0.wireOp",EDGE,"E7");var subQ2=sQuery(id+"F0.wireOp",EDGE,"E6");var subQ3=sQuery(id+"F0.wireOp",EDGE,"E5");var subQ4=sQuery(id+"F0.wireOp",EDGE,"E4");var subQ5=sQuery(id+"F0.wireOp",EDGE,"E22.filletArc");var subQ6=sQuery(id+"F0.wireOp",EDGE,"E1.bottom");var subQ7=sQuery(id+"F0.wireOp",EDGE,"E1.right");var subQ8=sQuery(id+"F0.wireOp",EDGE,"E1.top");var subQ9=sQuery(id+"F0.wireOp",EDGE,"E1.left");var subQ10=sQuery(id+"F0.wireOp",EDGE,"E23.filletArc");var subQ11=sQuery(id+"F0.wireOp",EDGE,"E24.filletArc");Q0=makeQuery(id+"F2.boolean.opBoolean","SPLIT",FACE,{"disambiguationData":[TD([makeQuery(id+"F1.opExtrude","SWEPT_FACE",FACE,{"disambiguationData":[OSD([subQ6])]})])],"derivedFrom":makeQuery(id+"F1.opExtrude","CAP_FACE",FACE,{"disambiguationData":[OSD([subQ6,subQ8,subQ9,subQ7,subQ4,subQ3,subQ2,subQ1,subQ0,subQ5,subQ10,subQ11])],"isStart":true})});}
            var sketch = newSketch(context, id + "F16", { "sketchPlane" : qUnion([Q0])});
            skLineSegment(sketch, "E79", {"start": v(0, 90) * mm, "end": v(0, 120) * mm, "construction": true});
            skCircle(sketch, "E80", {"center": v(0, 120) * mm, "radius": 6 * mm});
            skLineSegment(sketch, "E81", {"start": v(-33, 90) * mm, "end": v(-15, 108) * mm});
            skLineSegment(sketch, "E82", {"start": v(-15, 108) * mm, "end": v(-15, 120) * mm});
            skLineSegment(sketch, "E83", {"start": v(33, 90) * mm, "end": v(15, 108) * mm});
            skLineSegment(sketch, "E84", {"start": v(15, 108) * mm, "end": v(15, 120) * mm});
            skArc(sketch, "E85", {"start": v(15, 120) * mm, "mid": v(0, 135) * mm, "end": v(-15, 120) * mm});
            skPoint(sketch, "E86.endSnap0", {"position": v(80, 0) * mm});
            skLineSegment(sketch, "E87", {"start": v(-80, 0) * mm, "end": v(80, 0) * mm, "construction": true});
            skLineSegment(sketch, "E88.MirrorCS", {"start": v(33, -90) * mm, "end": v(15, -108) * mm});
            skLineSegment(sketch, "E89.MirrorCS", {"start": v(15, -108) * mm, "end": v(15, -120) * mm});
            skArc(sketch, "E90.MirrorCS", {"start": v(15, -120) * mm, "mid": v(0, -135) * mm, "end": v(-15, -120) * mm});
            skLineSegment(sketch, "E91.MirrorCS", {"start": v(-33, -90) * mm, "end": v(-15, -108) * mm});
            skLineSegment(sketch, "E92.MirrorCS", {"start": v(0, -90) * mm, "end": v(0, -120) * mm, "construction": true});
            skCircle(sketch, "E93.MirrorC", {"center": v(0, -120) * mm, "radius": 6 * mm});
            skLineSegment(sketch, "E94.MirrorCS", {"start": v(-15, -108) * mm, "end": v(-15, -120) * mm});
            skSolve(sketch);
        }
        {
            var Q0;
            Q0=makeQuery(id+"F16.imprint","IMPRINT",FACE,{"disambiguationData":[TD([[makeQuery(id+"F16.imprint","IMPRINT",EDGE,{"derivedFrom":makeQuery(id+"F1.opExtrude","CAP_EDGE",EDGE,{"disambiguationData":[OSD([sQuery(id+"F0.wireOp",EDGE,"E1.left")])],"isStart":true})}),-1.0]])]});
            var Q1;
            Q1=makeQuery(id+"F16.imprint","IMPRINT",FACE,{"disambiguationData":[TD([[makeQuery(id+"F16.imprint","IMPRINT",EDGE,{"derivedFrom":sQuery(id+"F16.wireOp",EDGE,"E80")}),-1.0]])]});
            var Q2;
            {var subQ1=sQuery(id+"F16.wireOp",EDGE,"E88.MirrorCS");Q2=makeQuery(id+"F16.imprint","IMPRINT",FACE,{"disambiguationData":[TD([[makeQuery(id+"F16.imprint","IMPRINT",EDGE,{"derivedFrom":subQ1}),-1.0]])]});}
            var Q3;
            Q3=makeQuery(id+"F2.opExtrude","CAP_FACE",FACE,{"disambiguationData":[OSD([sQuery(id+"F0.wireOp",EDGE,"E12"),sQuery(id+"F0.wireOp",EDGE,"E13"),sQuery(id+"F0.wireOp",EDGE,"E14"),sQuery(id+"F0.wireOp",EDGE,"E15"),sQuery(id+"F0.wireOp",EDGE,"E17.filletArc"),sQuery(id+"F0.wireOp",EDGE,"E18.filletArc"),sQuery(id+"F0.wireOp",EDGE,"E19.filletArc"),sQuery(id+"F0.wireOp",EDGE,"E20.filletArc"),sQuery(id+"F0.wireOp",EDGE,"E25.0"),sQuery(id+"F0.wireOp",EDGE,"E25.1"),sQuery(id+"F0.wireOp",EDGE,"E25.2"),sQuery(id+"F0.wireOp",EDGE,"E25.3"),sQuery(id+"F0.wireOp",EDGE,"E25.4"),sQuery(id+"F0.wireOp",EDGE,"E25.5"),sQuery(id+"F0.wireOp",EDGE,"E25.6"),sQuery(id+"F0.wireOp",EDGE,"E25.7")])],"isStart":false});
            extrude(context, id + "F17", {"entities" : qUnion([Q0, Q1, Q2]), "endBound" : BoundingType.UP_TO_SURFACE, "endBoundEntityFace" : qUnion([Q3]), "depth" : 25 * mm});
        }
    });
